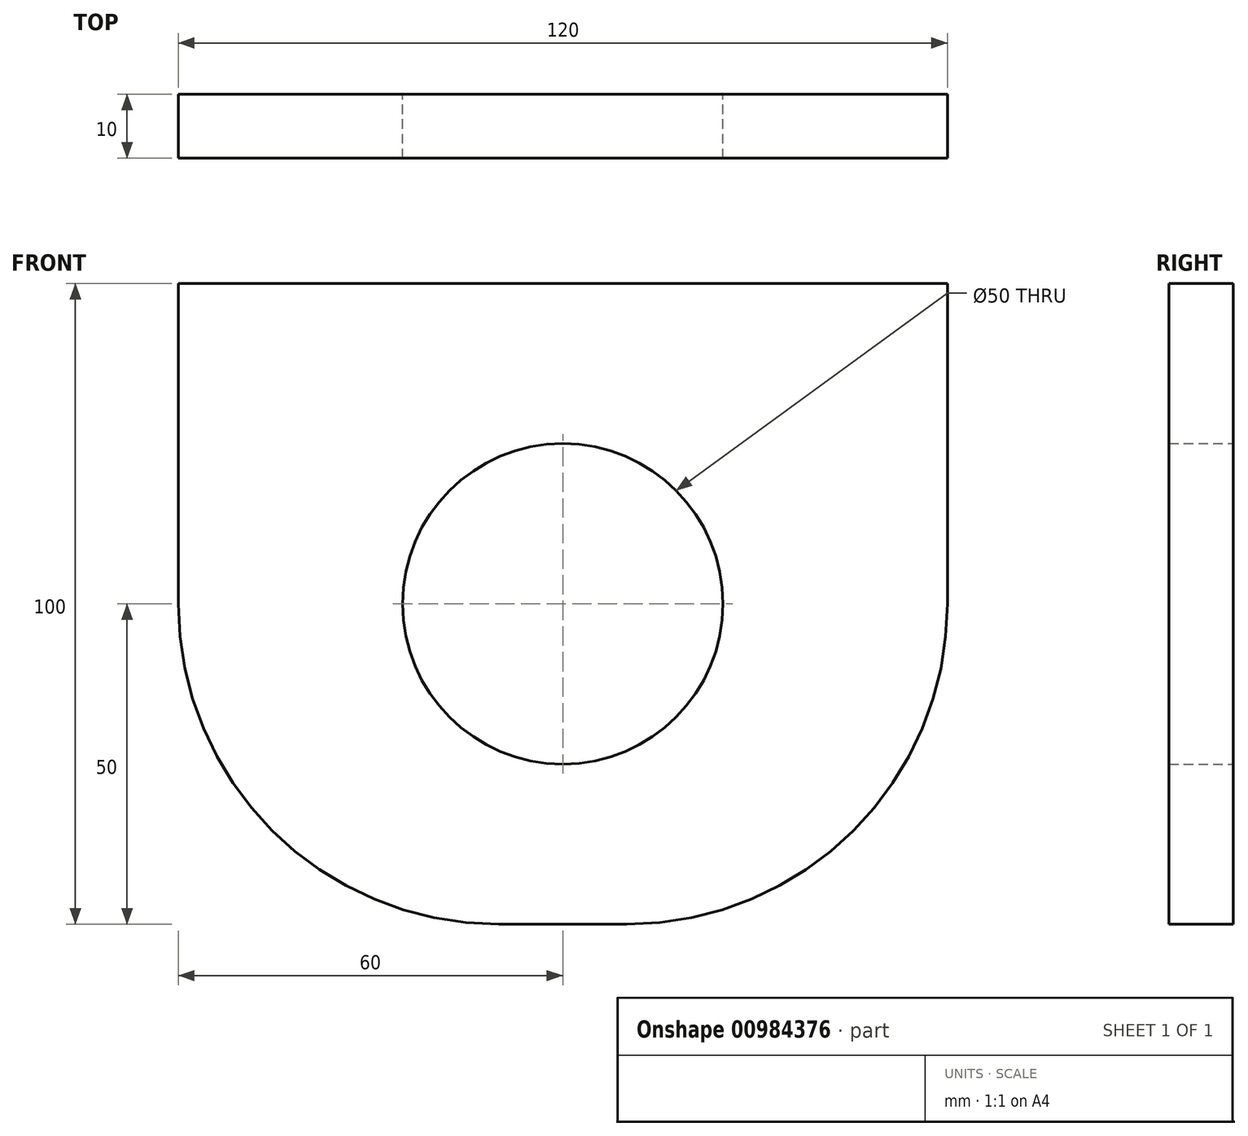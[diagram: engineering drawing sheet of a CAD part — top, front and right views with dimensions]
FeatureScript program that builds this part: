
annotation { "Feature Type Name" : "Feature", "Feature Type Description" : "" }
export const myFeature = defineFeature(function(context is Context, id is Id, definition is map)
    precondition{}
    {
        {
            var Q0;
            Q0=qCreatedBy(makeId("Front.planeOp"),FACE);
            var sketch = newSketch(context, id + "F0", { "sketchPlane" : qUnion([Q0])});
            skLineSegment(sketch, "E0.bottom", {"start": v(60, 50) * mm, "end": v(-60, 50) * mm});
            skLineSegment(sketch, "E0.top", {"start": v(60, -50) * mm, "end": v(-60, -50) * mm});
            skLineSegment(sketch, "E0.left", {"start": v(60, 50) * mm, "end": v(60, -50) * mm});
            skLineSegment(sketch, "E0.right", {"start": v(-60, 50) * mm, "end": v(-60, -50) * mm});
            skPoint(sketch, "E0.middle", {"position": v(0, 0) * mm});
            skCircle(sketch, "E1", {"center": v(0, 0) * mm, "radius": 25 * mm});
            skSolve(sketch);
        }
        {
            var Q0;
            Q0=makeQuery(id+"F0.imprint","IMPRINT",FACE,{"disambiguationData":[TD([[makeQuery(id+"F0.imprint","IMPRINT",EDGE,{"derivedFrom":sQuery(id+"F0.wireOp",EDGE,"E0.bottom")}),1.0]])]});
            extrude(context, id + "F1", {"entities" : qUnion([Q0]), "depth" : 10 * mm, "offsetDistance" : 25 * mm});
        }
        {
            var Q0;
            Q0=makeQuery(id+"F1.opExtrude","SWEPT_EDGE",EDGE,{"disambiguationData":[OSD([sQuery(id+"F0.wireOp",EDGE,"E0.top"),sQuery(id+"F0.wireOp",EDGE,"E0.right")])]});
            var Q1;
            Q1=makeQuery(id+"F1.opExtrude","SWEPT_EDGE",EDGE,{"disambiguationData":[OSD([sQuery(id+"F0.wireOp",EDGE,"E0.top"),sQuery(id+"F0.wireOp",EDGE,"E0.left")])]});
            fillet(context, id + "F2", {"entities" : qUnion([Q0, Q1]), "radius" : 50 * mm, "tangentPropagation" : true, "allowEdgeOverflow" : false});
        }
    });
